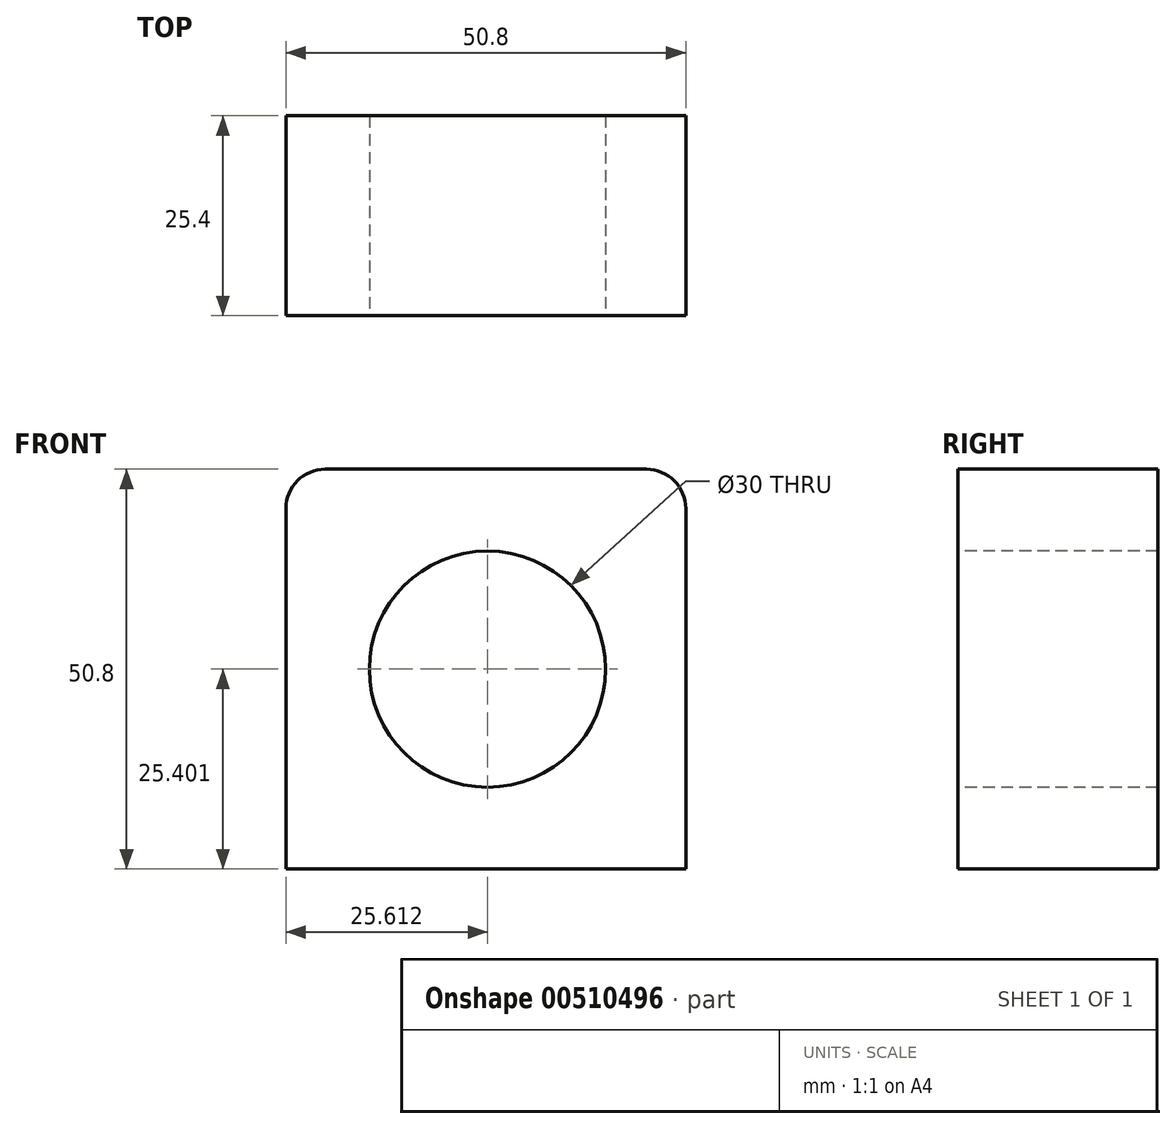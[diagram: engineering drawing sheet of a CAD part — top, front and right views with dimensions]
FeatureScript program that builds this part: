
annotation { "Feature Type Name" : "Feature", "Feature Type Description" : "" }
export const myFeature = defineFeature(function(context is Context, id is Id, definition is map)
    precondition{}
    {
        {
            var Q0;
            Q0=qCreatedBy(makeId("Front.planeOp"),FACE);
            var sketch = newSketch(context, id + "F0", { "sketchPlane" : qUnion([Q0])});
            skLineSegment(sketch, "E0.bottom", {"start": v(-50.8, 50.8) * mm, "end": v(0, 50.8) * mm});
            skLineSegment(sketch, "E0.top", {"start": v(-50.8, 0) * mm, "end": v(0, 0) * mm});
            skLineSegment(sketch, "E0.left", {"start": v(-50.8, 50.8) * mm, "end": v(-50.8, 0) * mm});
            skLineSegment(sketch, "E0.right", {"start": v(0, 50.8) * mm, "end": v(0, 0) * mm});
            skSolve(sketch);
        }
        {
            var Q0;
            Q0=makeQuery(id+"F0.imprint","IMPRINT",FACE,{"disambiguationData":[TD([[makeQuery(id+"F0.imprint","IMPRINT",EDGE,{"derivedFrom":sQuery(id+"F0.wireOp",EDGE,"E0.bottom")}),-1.0]])]});
            extrude(context, id + "F1", {"entities" : qUnion([Q0]), "depth" : 25.4 * mm});
        }
        {
            var Q0;
            Q0=makeQuery(id+"F1.opExtrude","SWEPT_EDGE",EDGE,{"disambiguationData":[OSD([sQuery(id+"F0.wireOp",EDGE,"E0.bottom"),sQuery(id+"F0.wireOp",EDGE,"E0.left")])]});
            fillet(context, id + "F2", {"entities" : qUnion([Q0]), "radius" : 5 * mm, "tangentPropagation" : true, "allowEdgeOverflow" : false});
        }
        {
            var Q0;
            Q0=makeQuery(id+"F1.opExtrude","SWEPT_EDGE",EDGE,{"disambiguationData":[OSD([sQuery(id+"F0.wireOp",EDGE,"E0.bottom"),sQuery(id+"F0.wireOp",EDGE,"E0.right")])]});
            fillet(context, id + "F3", {"entities" : qUnion([Q0]), "radius" : 5 * mm, "tangentPropagation" : true, "allowEdgeOverflow" : false});
        }
        {
            var Q0;
            Q0=makeQuery(id+"F1.opExtrude","CAP_FACE",FACE,{"disambiguationData":[OSD([sQuery(id+"F0.wireOp",EDGE,"E0.bottom"),sQuery(id+"F0.wireOp",EDGE,"E0.top"),sQuery(id+"F0.wireOp",EDGE,"E0.left"),sQuery(id+"F0.wireOp",EDGE,"E0.right")])],"isStart":false});
            var sketch = newSketch(context, id + "F4", { "sketchPlane" : qUnion([Q0])});
            skLineSegment(sketch, "E1", {"start": v(-25.4, 50.8) * mm, "end": v(-24.98, 0) * mm, "construction": true});
            skCircle(sketch, "E2", {"center": v(-25.19, 25.4) * mm, "radius": 15 * mm});
            skSolve(sketch);
        }
        {
            var Q0;
            Q0=makeQuery(id+"F4.imprint","IMPRINT",FACE,{"disambiguationData":[TD([[makeQuery(id+"F4.imprint","IMPRINT",EDGE,{"derivedFrom":sQuery(id+"F4.wireOp",EDGE,"E2")}),1.0]])]});
            var Q1;
            Q1=sQuery(id+"F4.wireOp",EDGE,"E2");
            var Q2;
            Q2=makeQuery(id+"F1.opExtrude","CAP_FACE",FACE,{"disambiguationData":[OSD([sQuery(id+"F0.wireOp",EDGE,"E0.bottom"),sQuery(id+"F0.wireOp",EDGE,"E0.top"),sQuery(id+"F0.wireOp",EDGE,"E0.left"),sQuery(id+"F0.wireOp",EDGE,"E0.right")])],"isStart":true});
            extrude(context, id + "F5", {"entities" : qUnion([Q0]), "operationType" : NewBodyOperationType.REMOVE, "surfaceEntities" : qUnion([Q1]), "endBound" : BoundingType.UP_TO_SURFACE, "oppositeDirection" : true, "endBoundEntityFace" : qUnion([Q2]), "depth" : 25 * mm});
        }
    });
